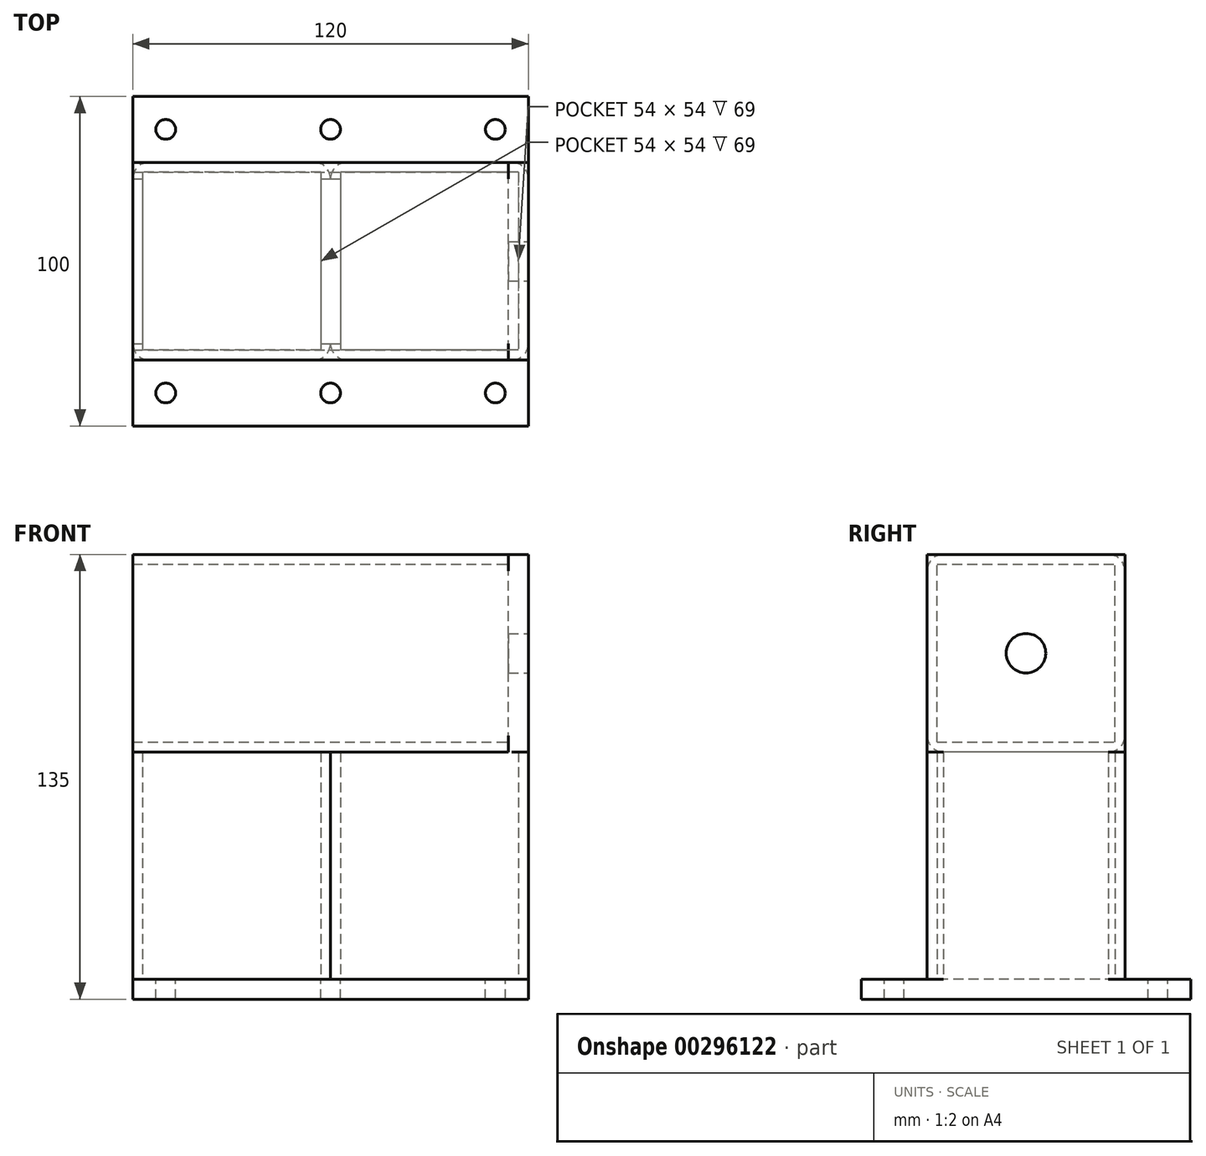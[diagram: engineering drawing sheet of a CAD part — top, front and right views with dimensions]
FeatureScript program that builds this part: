
annotation { "Feature Type Name" : "Feature", "Feature Type Description" : "" }
export const myFeature = defineFeature(function(context is Context, id is Id, definition is map)
    precondition{}
    {
        {
            var Q0;
            Q0=qCreatedBy(makeId("Top.planeOp"),FACE);
            var sketch = newSketch(context, id + "F0", { "sketchPlane" : qUnion([Q0])});
            skLineSegment(sketch, "E0.bottom", {"start": v(-15.85, -3.6) * mm, "end": v(-65.85, -3.6) * mm});
            skLineSegment(sketch, "E0.top", {"start": v(-15.85, -63.6) * mm, "end": v(-65.85, -63.6) * mm});
            skLineSegment(sketch, "E0.left", {"start": v(-10.85, -8.6) * mm, "end": v(-10.85, -58.6) * mm});
            skLineSegment(sketch, "E0.right", {"start": v(-70.85, -8.6) * mm, "end": v(-70.85, -58.6) * mm});
            skPoint(sketch, "E0.middle", {"position": v(-40.85, -33.6) * mm});
            skPoint(sketch, "E1.visualSharp", {"position": v(-70.85, -3.6) * mm});
            skArc(sketch, "E1.filletArc", {"start": v(-65.85, -3.6) * mm, "mid": v(-69.39, -5.06) * mm, "end": v(-70.85, -8.6) * mm});
            skPoint(sketch, "E2.visualSharp", {"position": v(-10.85, -3.6) * mm});
            skArc(sketch, "E2.filletArc", {"start": v(-10.85, -8.6) * mm, "mid": v(-12.31, -5.06) * mm, "end": v(-15.85, -3.6) * mm});
            skPoint(sketch, "E3.visualSharp", {"position": v(-10.85, -63.6) * mm});
            skArc(sketch, "E3.filletArc", {"start": v(-15.85, -63.6) * mm, "mid": v(-12.31, -62.13) * mm, "end": v(-10.85, -58.6) * mm});
            skPoint(sketch, "E4.visualSharp", {"position": v(-70.85, -63.6) * mm});
            skArc(sketch, "E4.filletArc", {"start": v(-70.85, -58.6) * mm, "mid": v(-69.39, -62.13) * mm, "end": v(-65.85, -63.6) * mm});
            skLineSegment(sketch, "E5.0", {"start": v(-67.85, -6.6) * mm, "end": v(-67.85, -60.6) * mm});
            skLineSegment(sketch, "E5.1", {"start": v(-13.85, -6.6) * mm, "end": v(-67.85, -6.6) * mm});
            skLineSegment(sketch, "E5.2", {"start": v(-13.85, -6.6) * mm, "end": v(-13.85, -60.6) * mm});
            skLineSegment(sketch, "E5.3", {"start": v(-13.85, -60.6) * mm, "end": v(-67.85, -60.6) * mm});
            skLineSegment(sketch, "E6.bottom", {"start": v(44.15, -3.6) * mm, "end": v(-5.85, -3.6) * mm});
            skLineSegment(sketch, "E6.top", {"start": v(44.15, -63.6) * mm, "end": v(-5.85, -63.6) * mm});
            skLineSegment(sketch, "E6.left", {"start": v(49.15, -8.6) * mm, "end": v(49.15, -58.6) * mm});
            skPoint(sketch, "E6.middle", {"position": v(19.15, -33.6) * mm});
            skArc(sketch, "E7.filletArc", {"start": v(-5.85, -3.6) * mm, "mid": v(-9.39, -5.06) * mm, "end": v(-10.85, -8.6) * mm});
            skPoint(sketch, "E8.visualSharp", {"position": v(49.15, -3.6) * mm});
            skArc(sketch, "E8.filletArc", {"start": v(49.15, -8.6) * mm, "mid": v(47.69, -5.06) * mm, "end": v(44.15, -3.6) * mm});
            skPoint(sketch, "E9.visualSharp", {"position": v(49.15, -63.6) * mm});
            skArc(sketch, "E9.filletArc", {"start": v(44.15, -63.6) * mm, "mid": v(47.69, -62.13) * mm, "end": v(49.15, -58.6) * mm});
            skArc(sketch, "E10.filletArc", {"start": v(-10.85, -58.6) * mm, "mid": v(-9.39, -62.13) * mm, "end": v(-5.85, -63.6) * mm});
            skLineSegment(sketch, "E11.0", {"start": v(-7.85, -6.6) * mm, "end": v(-7.85, -60.6) * mm});
            skLineSegment(sketch, "E11.1", {"start": v(46.15, -6.6) * mm, "end": v(-7.85, -6.6) * mm});
            skLineSegment(sketch, "E11.2", {"start": v(46.15, -6.6) * mm, "end": v(46.15, -60.6) * mm});
            skLineSegment(sketch, "E11.3", {"start": v(46.15, -60.6) * mm, "end": v(-7.85, -60.6) * mm});
            skLineSegment(sketch, "E12.bottom", {"start": v(104.15, -3.6) * mm, "end": v(54.15, -3.6) * mm});
            skLineSegment(sketch, "E12.top", {"start": v(104.15, -63.6) * mm, "end": v(54.15, -63.6) * mm});
            skLineSegment(sketch, "E12.left", {"start": v(109.15, -8.6) * mm, "end": v(109.15, -58.6) * mm});
            skPoint(sketch, "E12.middle", {"position": v(79.15, -33.6) * mm});
            skArc(sketch, "E13.filletArc", {"start": v(54.15, -3.6) * mm, "mid": v(50.61, -5.06) * mm, "end": v(49.15, -8.6) * mm});
            skPoint(sketch, "E14.visualSharp", {"position": v(109.15, -3.6) * mm});
            skArc(sketch, "E14.filletArc", {"start": v(109.15, -8.6) * mm, "mid": v(107.69, -5.06) * mm, "end": v(104.15, -3.6) * mm});
            skPoint(sketch, "E15.visualSharp", {"position": v(109.15, -63.6) * mm});
            skArc(sketch, "E15.filletArc", {"start": v(104.15, -63.6) * mm, "mid": v(107.69, -62.13) * mm, "end": v(109.15, -58.6) * mm});
            skArc(sketch, "E16.filletArc", {"start": v(49.15, -58.6) * mm, "mid": v(50.61, -62.13) * mm, "end": v(54.15, -63.6) * mm});
            skLineSegment(sketch, "E17.0", {"start": v(52.15, -6.6) * mm, "end": v(52.15, -60.6) * mm});
            skLineSegment(sketch, "E17.1", {"start": v(106.15, -6.6) * mm, "end": v(52.15, -6.6) * mm});
            skLineSegment(sketch, "E17.2", {"start": v(106.15, -6.6) * mm, "end": v(106.15, -60.6) * mm});
            skLineSegment(sketch, "E17.3", {"start": v(106.15, -60.6) * mm, "end": v(52.15, -60.6) * mm});
            skSolve(sketch);
        }
        {
            var Q0;
            Q0=makeQuery(id+"F0.imprint","IMPRINT",FACE,{"disambiguationData":[TD([[makeQuery(id+"F0.imprint","IMPRINT",EDGE,{"derivedFrom":sQuery(id+"F0.wireOp",EDGE,"E6.bottom")}),1.0]])]});
            var Q1;
            Q1=makeQuery(id+"F0.imprint","IMPRINT",FACE,{"disambiguationData":[TD([[makeQuery(id+"F0.imprint","IMPRINT",EDGE,{"derivedFrom":sQuery(id+"F0.wireOp",EDGE,"E12.bottom")}),1.0]])]});
            extrude(context, id + "F1", {"entities" : qUnion([Q0, Q1]), "depth" : 69 * mm});
        }
        {
            var Q0;
            Q0=makeQuery(id+"F1.opExtrude","CAP_FACE",FACE,{"disambiguationData":[OSD([sQuery(id+"F0.wireOp",EDGE,"E0.bottom"),sQuery(id+"F0.wireOp",EDGE,"E0.top"),sQuery(id+"F0.wireOp",EDGE,"E0.right"),sQuery(id+"F0.wireOp",EDGE,"E1.filletArc"),sQuery(id+"F0.wireOp",EDGE,"E2.filletArc"),sQuery(id+"F0.wireOp",EDGE,"E3.filletArc"),sQuery(id+"F0.wireOp",EDGE,"E4.filletArc"),sQuery(id+"F0.wireOp",EDGE,"E5.0"),sQuery(id+"F0.wireOp",EDGE,"E5.1"),sQuery(id+"F0.wireOp",EDGE,"E5.2"),sQuery(id+"F0.wireOp",EDGE,"E5.3"),sQuery(id+"F0.wireOp",EDGE,"E6.bottom"),sQuery(id+"F0.wireOp",EDGE,"E6.top"),sQuery(id+"F0.wireOp",EDGE,"E7.filletArc"),sQuery(id+"F0.wireOp",EDGE,"E8.filletArc"),sQuery(id+"F0.wireOp",EDGE,"E9.filletArc"),sQuery(id+"F0.wireOp",EDGE,"E10.filletArc"),sQuery(id+"F0.wireOp",EDGE,"E11.0"),sQuery(id+"F0.wireOp",EDGE,"E11.1"),sQuery(id+"F0.wireOp",EDGE,"E11.2"),sQuery(id+"F0.wireOp",EDGE,"E11.3"),sQuery(id+"F0.wireOp",EDGE,"E12.bottom"),sQuery(id+"F0.wireOp",EDGE,"E12.top"),sQuery(id+"F0.wireOp",EDGE,"E12.left"),sQuery(id+"F0.wireOp",EDGE,"E13.filletArc"),sQuery(id+"F0.wireOp",EDGE,"E14.filletArc"),sQuery(id+"F0.wireOp",EDGE,"E15.filletArc"),sQuery(id+"F0.wireOp",EDGE,"E16.filletArc"),sQuery(id+"F0.wireOp",EDGE,"E17.0"),sQuery(id+"F0.wireOp",EDGE,"E17.1"),sQuery(id+"F0.wireOp",EDGE,"E17.2"),sQuery(id+"F0.wireOp",EDGE,"E17.3")])],"isStart":true});
            var sketch = newSketch(context, id + "F2", { "sketchPlane" : qUnion([Q0])});
            skLineSegment(sketch, "E18.bottom", {"start": v(109.15, -16.4) * mm, "end": v(-10.85, -16.4) * mm});
            skLineSegment(sketch, "E18.top", {"start": v(109.15, 83.6) * mm, "end": v(-10.85, 83.6) * mm});
            skLineSegment(sketch, "E18.left", {"start": v(109.15, -16.4) * mm, "end": v(109.15, 83.6) * mm});
            skLineSegment(sketch, "E18.right", {"start": v(-10.85, -16.4) * mm, "end": v(-10.85, 83.6) * mm});
            skCircle(sketch, "E19", {"center": v(99.15, 73.6) * mm, "radius": 3 * mm});
            skCircle(sketch, "E20", {"center": v(-0.85, 73.6) * mm, "radius": 3 * mm});
            skCircle(sketch, "E21", {"center": v(-0.85, -6.4) * mm, "radius": 3 * mm});
            skCircle(sketch, "E22", {"center": v(49.15, -6.4) * mm, "radius": 3 * mm});
            skCircle(sketch, "E23", {"center": v(99.15, -6.4) * mm, "radius": 3 * mm});
            skCircle(sketch, "E24", {"center": v(49.15, 73.6) * mm, "radius": 3 * mm});
            skSolve(sketch);
        }
        {
            var Q0;
            {var subQ2=sQuery(id+"F2.wireOp",EDGE,"E18.bottom");Q0=makeQuery(id+"F2.imprint","IMPRINT",FACE,{"disambiguationData":[TD([[makeQuery(id+"F2.imprint","IMPRINT",EDGE,{"derivedFrom":subQ2}),-1.0]])]});}
            var Q1;
            {var subQ1=sQuery(id+"F2.wireOp",EDGE,"E18.top");Q1=makeQuery(id+"F2.imprint","IMPRINT",FACE,{"disambiguationData":[TD([[makeQuery(id+"F2.imprint","IMPRINT",EDGE,{"derivedFrom":subQ1}),1.0]])]});}
            var Q2;
            Q2=makeQuery(id+"F2.imprint","IMPRINT",FACE,{"disambiguationData":[TD([[makeQuery(id+"F2.imprint","IMPRINT",EDGE,{"derivedFrom":makeQuery(id+"F1.opExtrude","CAP_EDGE",EDGE,{"disambiguationData":[OSD([sQuery(id+"F0.wireOp",EDGE,"E0.bottom")])],"isStart":true})}),-1.0]])]});
            var Q3;
            Q3=makeQuery(id+"F2.imprint","IMPRINT",FACE,{"disambiguationData":[TD([[makeQuery(id+"F2.imprint","IMPRINT",EDGE,{"derivedFrom":makeQuery(id+"F1.opExtrude","CAP_EDGE",EDGE,{"disambiguationData":[OSD([sQuery(id+"F0.wireOp",EDGE,"E6.bottom")])],"isStart":true})}),-1.0]])]});
            var Q4;
            Q4=makeQuery(id+"F2.imprint","IMPRINT",FACE,{"disambiguationData":[TD([[makeQuery(id+"F2.imprint","IMPRINT",EDGE,{"derivedFrom":makeQuery(id+"F1.opExtrude","CAP_EDGE",EDGE,{"disambiguationData":[OSD([sQuery(id+"F0.wireOp",EDGE,"E11.0")])],"isStart":true})}),-1.0]])]});
            var Q5;
            Q5=makeQuery(id+"F2.imprint","IMPRINT",FACE,{"disambiguationData":[TD([[makeQuery(id+"F2.imprint","IMPRINT",EDGE,{"derivedFrom":makeQuery(id+"F1.opExtrude","CAP_EDGE",EDGE,{"disambiguationData":[OSD([sQuery(id+"F0.wireOp",EDGE,"E17.0")])],"isStart":true})}),-1.0]])]});
            extrude(context, id + "F3", {"entities" : qUnion([Q0, Q1, Q2, Q3, Q4, Q5]), "operationType" : NewBodyOperationType.ADD, "depth" : 6 * mm});
        }
        {
            var Q0;
            Q0=makeQuery(id+"F3.boolean.opBoolean","MERGE",FACE,{"derivedFrom":[makeQuery(id+"F1.opExtrude","SWEPT_FACE",FACE,{"disambiguationData":[OSD([sQuery(id+"F0.wireOp",EDGE,"E12.left")])]}),makeQuery(id+"F3.opExtrude","SWEPT_FACE",FACE,{"disambiguationData":[OSD([sQuery(id+"F2.wireOp",EDGE,"E18.left")])]})]});
            var sketch = newSketch(context, id + "F4", { "sketchPlane" : qUnion([Q0])});
            skLineSegment(sketch, "E25.bottom", {"start": v(-8.6, 129) * mm, "end": v(-58.6, 129) * mm});
            skLineSegment(sketch, "E25.top", {"start": v(-8.6, 69) * mm, "end": v(-58.6, 69) * mm});
            skLineSegment(sketch, "E25.left", {"start": v(-3.6, 124) * mm, "end": v(-3.6, 74) * mm});
            skLineSegment(sketch, "E25.right", {"start": v(-63.6, 124) * mm, "end": v(-63.6, 74) * mm});
            skPoint(sketch, "E25.middle", {"position": v(-33.6, 99) * mm});
            skPoint(sketch, "E26.visualSharp", {"position": v(-63.6, 129) * mm});
            skArc(sketch, "E26.filletArc", {"start": v(-58.6, 129) * mm, "mid": v(-62.13, 127.54) * mm, "end": v(-63.6, 124) * mm});
            skPoint(sketch, "E27.visualSharp", {"position": v(-3.6, 129) * mm});
            skArc(sketch, "E27.filletArc", {"start": v(-3.6, 124) * mm, "mid": v(-5.06, 127.54) * mm, "end": v(-8.6, 129) * mm});
            skPoint(sketch, "E28.visualSharp", {"position": v(-3.6, 69) * mm});
            skArc(sketch, "E28.filletArc", {"start": v(-8.6, 69) * mm, "mid": v(-5.06, 70.46) * mm, "end": v(-3.6, 74) * mm});
            skPoint(sketch, "E29.visualSharp", {"position": v(-63.6, 69) * mm});
            skArc(sketch, "E29.filletArc", {"start": v(-63.6, 74) * mm, "mid": v(-62.13, 70.46) * mm, "end": v(-58.6, 69) * mm});
            skLineSegment(sketch, "E30.0", {"start": v(-60.6, 126) * mm, "end": v(-60.6, 72) * mm});
            skLineSegment(sketch, "E30.1", {"start": v(-6.6, 126) * mm, "end": v(-60.6, 126) * mm});
            skLineSegment(sketch, "E30.2", {"start": v(-6.6, 126) * mm, "end": v(-6.6, 72) * mm});
            skLineSegment(sketch, "E30.3", {"start": v(-6.6, 72) * mm, "end": v(-60.6, 72) * mm});
            skSolve(sketch);
        }
        {
            var Q0;
            Q0=makeQuery(id+"F4.imprint","IMPRINT",FACE,{"disambiguationData":[TD([[makeQuery(id+"F4.imprint","IMPRINT",EDGE,{"derivedFrom":sQuery(id+"F4.wireOp",EDGE,"E25.bottom")}),1.0]])]});
            var Q1;
            Q1=makeQuery(id+"F3.boolean.opBoolean","MERGE",FACE,{"derivedFrom":[makeQuery(id+"F1.opExtrude","SWEPT_FACE",FACE,{"disambiguationData":[OSD([sQuery(id+"F0.wireOp",EDGE,"E0.right")])]}),makeQuery(id+"F3.opExtrude","SWEPT_FACE",FACE,{"disambiguationData":[OSD([sQuery(id+"F2.wireOp",EDGE,"E18.right")])]})]});
            extrude(context, id + "F5", {"entities" : qUnion([Q0]), "operationType" : NewBodyOperationType.ADD, "endBound" : BoundingType.UP_TO_SURFACE, "oppositeDirection" : true, "endBoundEntityFace" : qUnion([Q1]), "depth" : 25 * mm});
        }
        {
            var Q0;
            Q0=makeQuery(id+"F5.boolean.opBoolean","MERGE",FACE,{"derivedFrom":[makeQuery(id+"F3.boolean.opBoolean","MERGE",FACE,{"derivedFrom":[makeQuery(id+"F1.opExtrude","SWEPT_FACE",FACE,{"disambiguationData":[OSD([sQuery(id+"F0.wireOp",EDGE,"E12.left")])]}),makeQuery(id+"F3.opExtrude","SWEPT_FACE",FACE,{"disambiguationData":[OSD([sQuery(id+"F2.wireOp",EDGE,"E18.left")])]})]}),makeQuery(id+"F5.opExtrude","CAP_FACE",FACE,{"disambiguationData":[OSD([sQuery(id+"F4.wireOp",EDGE,"E25.bottom"),sQuery(id+"F4.wireOp",EDGE,"E25.top"),sQuery(id+"F4.wireOp",EDGE,"E25.left"),sQuery(id+"F4.wireOp",EDGE,"E25.right"),sQuery(id+"F4.wireOp",EDGE,"E26.filletArc"),sQuery(id+"F4.wireOp",EDGE,"E27.filletArc"),sQuery(id+"F4.wireOp",EDGE,"E28.filletArc"),sQuery(id+"F4.wireOp",EDGE,"E29.filletArc"),sQuery(id+"F4.wireOp",EDGE,"E30.0"),sQuery(id+"F4.wireOp",EDGE,"E30.1"),sQuery(id+"F4.wireOp",EDGE,"E30.2"),sQuery(id+"F4.wireOp",EDGE,"E30.3")])],"isStart":true})]});
            var sketch = newSketch(context, id + "F6", { "sketchPlane" : qUnion([Q0])});
            skLineSegment(sketch, "E31.bottom", {"start": v(-3.6, 129) * mm, "end": v(-63.6, 129) * mm});
            skLineSegment(sketch, "E31.top", {"start": v(-3.6, 69) * mm, "end": v(-63.6, 69) * mm});
            skLineSegment(sketch, "E31.left", {"start": v(-3.6, 129) * mm, "end": v(-3.6, 69) * mm});
            skLineSegment(sketch, "E31.right", {"start": v(-63.6, 129) * mm, "end": v(-63.6, 69) * mm});
            skCircle(sketch, "E32", {"center": v(-33.6, 99) * mm, "radius": 6 * mm});
            skSolve(sketch);
        }
        {
            var Q0;
            Q0 = qSketchRegion(id + "F6", true);
            extrude(context, id + "F7", {"entities" : qUnion([Q0]), "operationType" : NewBodyOperationType.ADD, "oppositeDirection" : true, "depth" : 6 * mm});
        }
    });
